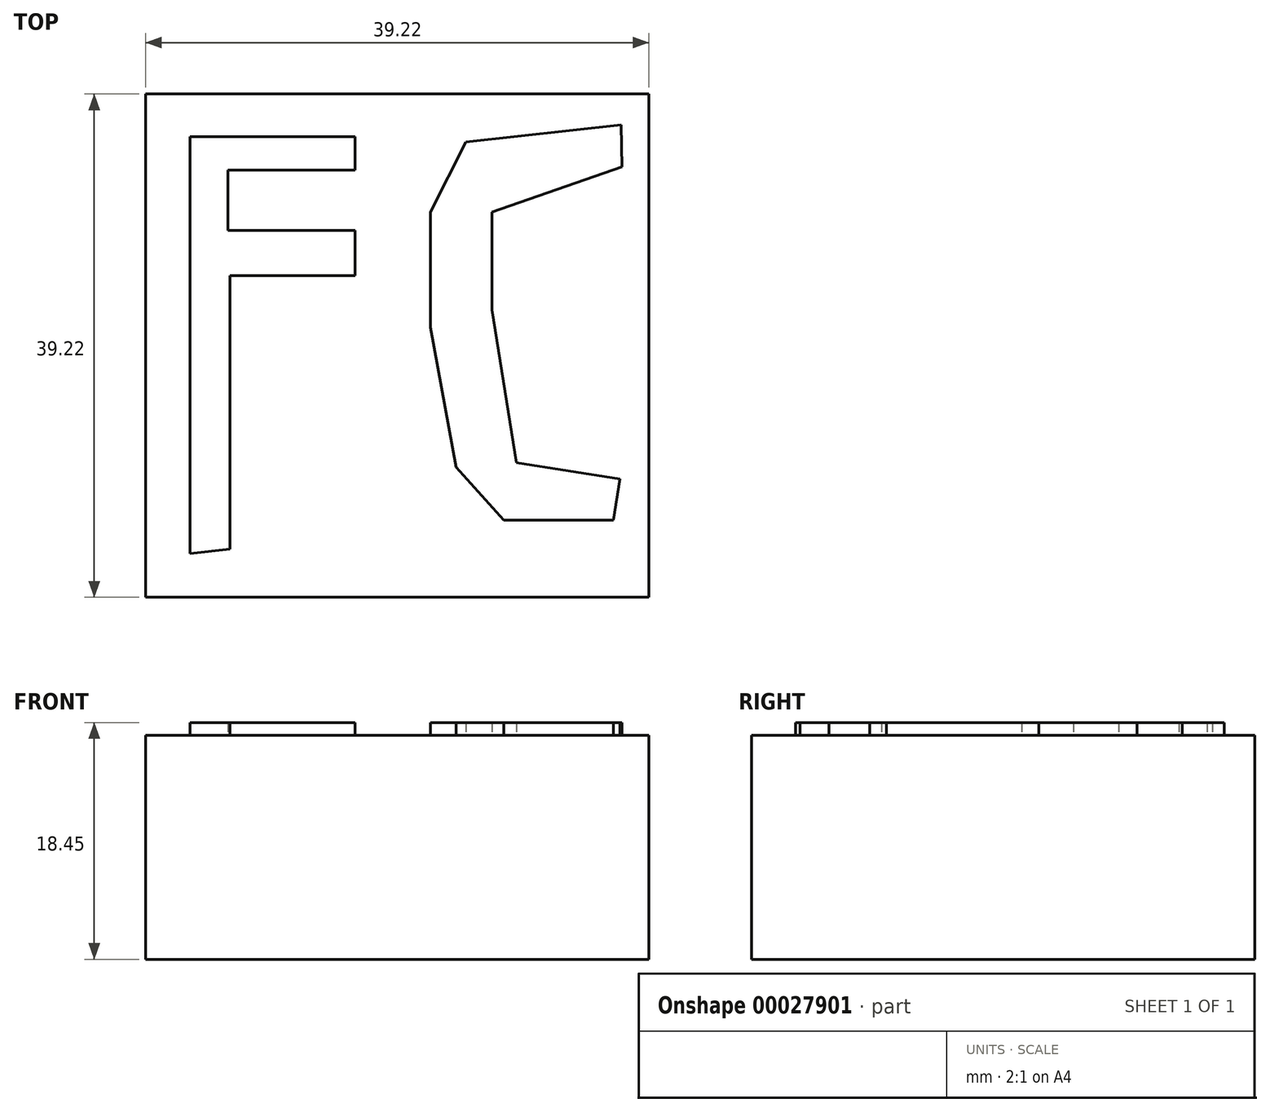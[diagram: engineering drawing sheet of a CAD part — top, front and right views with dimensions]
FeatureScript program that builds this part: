
annotation { "Feature Type Name" : "Feature", "Feature Type Description" : "" }
export const myFeature = defineFeature(function(context is Context, id is Id, definition is map)
    precondition{}
    {
        {
            var Q0;
            Q0=qCreatedBy(makeId("Top.planeOp"),FACE);
            var sketch = newSketch(context, id + "F0", { "sketchPlane" : qUnion([Q0])});
            skLineSegment(sketch, "E0.rect.bottom", {"start": v(19.6, 19.6) * mm, "end": v(-19.6, 19.6) * mm});
            skLineSegment(sketch, "E0.rect.top", {"start": v(19.6, -19.6) * mm, "end": v(-19.6, -19.6) * mm});
            skLineSegment(sketch, "E0.rect.left", {"start": v(19.6, 19.6) * mm, "end": v(19.6, -19.6) * mm});
            skLineSegment(sketch, "E0.rect.right", {"start": v(-19.6, 19.6) * mm, "end": v(-19.6, -19.6) * mm});
            skPoint(sketch, "E0.rect.middle", {"position": v(0, 0) * mm});
            skSolve(sketch);
        }
        {
            var Q0;
            Q0 = qSketchRegion(id + "F0", true);
            extrude(context, id + "F1", {"entities" : qUnion([Q0]), "depth" : 17.45 * mm});
        }
        {
            var Q0;
            Q0=makeQuery(id+"F1.opExtrude","CAP_FACE",FACE,{"disambiguationData":[OSD([sQuery(id+"F0.wireOp",EDGE,"E0.rect.bottom"),sQuery(id+"F0.wireOp",EDGE,"E0.rect.top"),sQuery(id+"F0.wireOp",EDGE,"E0.rect.left"),sQuery(id+"F0.wireOp",EDGE,"E0.rect.right")])],"isStart":false});
            var sketch = newSketch(context, id + "F2", { "sketchPlane" : qUnion([Q0])});
            skLineSegment(sketch, "E1", {"start": v(-16.14, -16.19) * mm, "end": v(-16.14, 16.3) * mm});
            skLineSegment(sketch, "E2", {"start": v(-16.14, 16.3) * mm, "end": v(-3.3, 16.3) * mm});
            skLineSegment(sketch, "E3", {"start": v(-3.3, 16.3) * mm, "end": v(-3.3, 13.7) * mm});
            skLineSegment(sketch, "E4", {"start": v(-3.3, 13.7) * mm, "end": v(-13.2, 13.7) * mm});
            skLineSegment(sketch, "E5", {"start": v(-13.2, 13.7) * mm, "end": v(-13.2, 9) * mm});
            skLineSegment(sketch, "E6", {"start": v(-13.2, 9) * mm, "end": v(-3.3, 9) * mm});
            skLineSegment(sketch, "E7", {"start": v(-3.3, 9) * mm, "end": v(-3.3, 5.47) * mm});
            skLineSegment(sketch, "E8", {"start": v(-3.3, 5.47) * mm, "end": v(-13.03, 5.47) * mm});
            skLineSegment(sketch, "E9", {"start": v(-13.03, 5.47) * mm, "end": v(-13.03, -15.85) * mm});
            skLineSegment(sketch, "E10", {"start": v(-13.03, -15.85) * mm, "end": v(-16.14, -16.19) * mm});
            skLineSegment(sketch, "E11", {"start": v(17.44, 17.22) * mm, "end": v(5.35, 15.87) * mm});
            skLineSegment(sketch, "E12", {"start": v(5.35, 15.87) * mm, "end": v(2.58, 10.42) * mm});
            skLineSegment(sketch, "E13", {"start": v(2.58, 10.42) * mm, "end": v(2.58, 1.44) * mm});
            skLineSegment(sketch, "E14", {"start": v(2.58, 1.44) * mm, "end": v(4.6, -9.47) * mm});
            skLineSegment(sketch, "E15", {"start": v(4.6, -9.47) * mm, "end": v(8.29, -13.59) * mm});
            skLineSegment(sketch, "E16", {"start": v(8.29, -13.59) * mm, "end": v(16.85, -13.59) * mm});
            skLineSegment(sketch, "E17", {"start": v(16.85, -13.59) * mm, "end": v(17.35, -10.4) * mm});
            skLineSegment(sketch, "E18", {"start": v(17.35, -10.4) * mm, "end": v(9.28, -9.12) * mm});
            skLineSegment(sketch, "E19", {"start": v(9.28, -9.12) * mm, "end": v(7.36, 2.78) * mm});
            skLineSegment(sketch, "E20", {"start": v(7.36, 2.78) * mm, "end": v(7.36, 10.42) * mm});
            skLineSegment(sketch, "E21", {"start": v(7.36, 10.42) * mm, "end": v(17.52, 13.94) * mm});
            skLineSegment(sketch, "E22", {"start": v(17.52, 13.94) * mm, "end": v(17.44, 17.22) * mm});
            skSolve(sketch);
        }
        {
            var Q0;
            Q0 = qSketchRegion(id + "F2", true);
            extrude(context, id + "F3", {"entities" : qUnion([Q0]), "operationType" : NewBodyOperationType.ADD, "depth" : 1 * mm});
        }
    });
